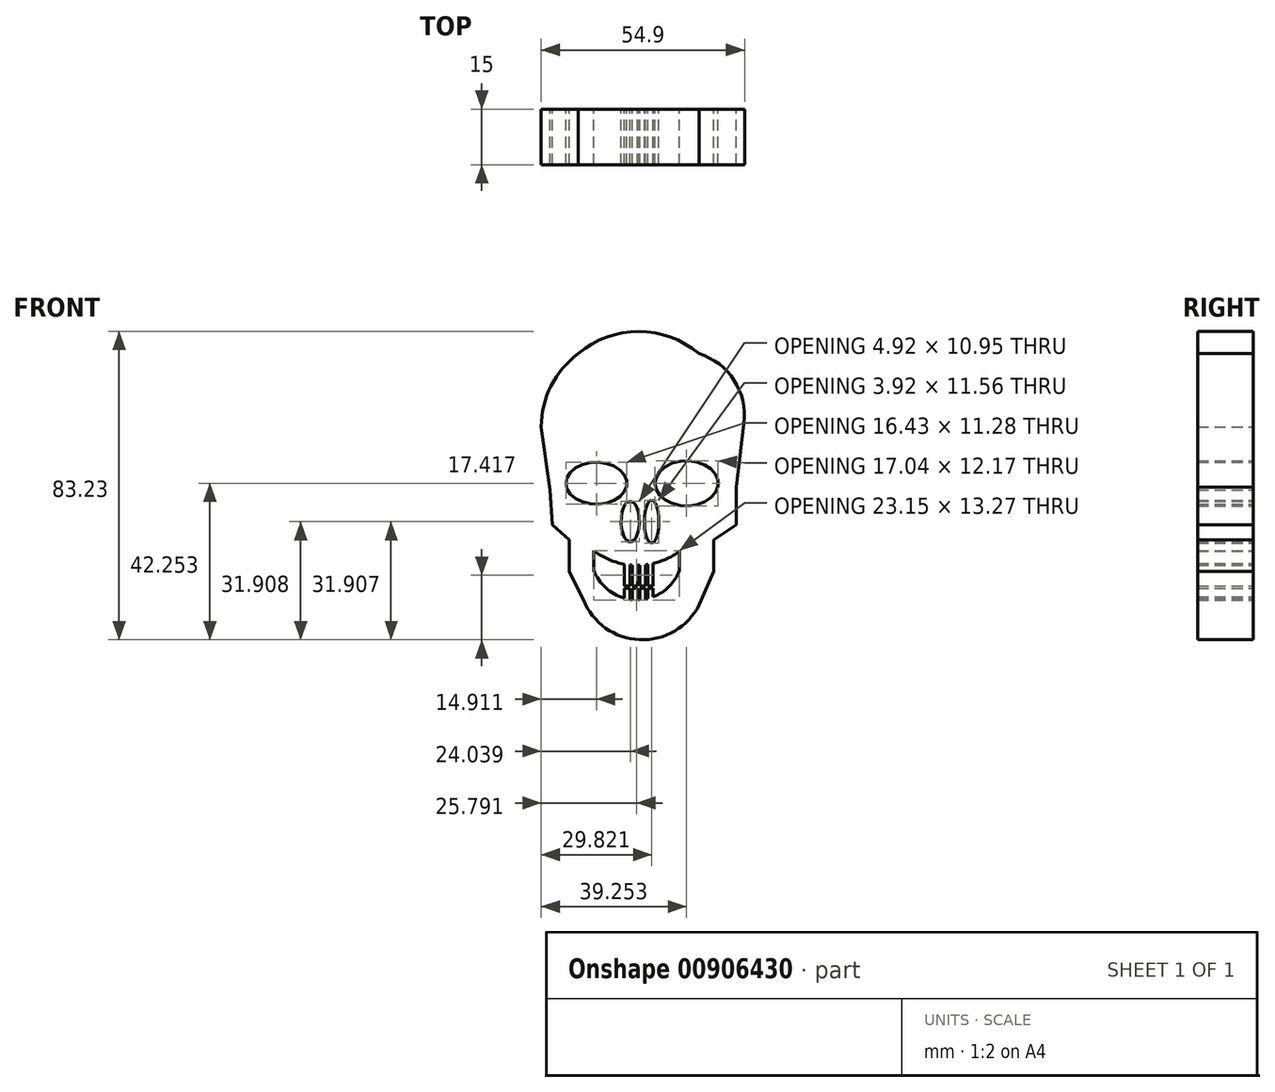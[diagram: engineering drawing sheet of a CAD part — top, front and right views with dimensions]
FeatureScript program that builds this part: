
annotation { "Feature Type Name" : "Feature", "Feature Type Description" : "" }
export const myFeature = defineFeature(function(context is Context, id is Id, definition is map)
    precondition{}
    {
        {
            var Q0;
            Q0=qCreatedBy(makeId("Front.planeOp"),FACE);
            var sketch = newSketch(context, id + "F0", { "sketchPlane" : qUnion([Q0])});
            skArc(sketch, "E0", {"start": v(-11.85, 27.42) * mm, "mid": v(-19.21, 18.72) * mm, "end": v(-21.89, 7.64) * mm});
            skArc(sketch, "E1", {"start": v(20.71, 27.42) * mm, "mid": v(4.43, 33.4) * mm, "end": v(-11.85, 27.42) * mm});
            skArc(sketch, "E2", {"start": v(32.88, 8.55) * mm, "mid": v(30.21, 20.19) * mm, "end": v(20.71, 27.42) * mm});
            skLineSegment(sketch, "E3", {"start": v(-21.89, 7.64) * mm, "end": v(-19.45, -9.4) * mm});
            skLineSegment(sketch, "E4", {"start": v(32.88, 8.55) * mm, "end": v(30.78, -8.64) * mm});
            skArc(sketch, "E5", {"start": v(-10.02, -40.13) * mm, "mid": v(5.94, -49.82) * mm, "end": v(21.32, -39.22) * mm});
            skLineSegment(sketch, "E6", {"start": v(-14.28, -22.8) * mm, "end": v(-14.28, -31.31) * mm});
            skLineSegment(sketch, "E7", {"start": v(-14.28, -31.31) * mm, "end": v(-10.02, -40.13) * mm});
            skLineSegment(sketch, "E8", {"start": v(24.67, -22.8) * mm, "end": v(24.67, -31.31) * mm});
            skLineSegment(sketch, "E9", {"start": v(24.67, -31.31) * mm, "end": v(21.32, -39.22) * mm});
            skLineSegment(sketch, "E10", {"start": v(-13.98, 3.99) * mm, "end": v(-16.72, 11.9) * mm});
            skLineSegment(sketch, "E11", {"start": v(-16.72, 11.9) * mm, "end": v(-13.98, 3.99) * mm});
            skLineSegment(sketch, "E12", {"start": v(-13.98, 3.99) * mm, "end": v(-19.45, -9.4) * mm});
            skLineSegment(sketch, "E13", {"start": v(25.27, 3.99) * mm, "end": v(27.4, 11.9) * mm});
            skLineSegment(sketch, "E14", {"start": v(27.4, 11.9) * mm, "end": v(25.27, 3.99) * mm});
            skLineSegment(sketch, "E15", {"start": v(25.27, 3.99) * mm, "end": v(30.78, -8.64) * mm});
            skLineSegment(sketch, "E16", {"start": v(-14.28, -22.8) * mm, "end": v(-18.85, -18.84) * mm});
            skLineSegment(sketch, "E17", {"start": v(-19.45, -9.4) * mm, "end": v(-18.85, -18.84) * mm});
            skLineSegment(sketch, "E18", {"start": v(24.67, -22.8) * mm, "end": v(30.78, -18.84) * mm});
            skLineSegment(sketch, "E19", {"start": v(30.78, -8.64) * mm, "end": v(30.78, -18.84) * mm});
            skEllipse(sketch, "E20", {"center": v(17.36, -7.58) * mm, "majorRadius": 8.52 * mm, "minorRadius": 6.09 * mm, "majorAxis": v(-1, 0)});
            skEllipse(sketch, "E21", {"center": v(-6.98, -7.58) * mm, "majorRadius": 8.22 * mm, "minorRadius": 5.64 * mm, "majorAxis": v(-1, 0)});
            skPoint(sketch, "E21.centerSnap0", {"position": v(8.84, -7.58) * mm});
            skEllipse(sketch, "E22", {"center": v(7.93, -17.92) * mm, "majorRadius": 5.78 * mm, "minorRadius": 1.96 * mm, "majorAxis": v(0, 1)});
            skEllipse(sketch, "E23", {"center": v(2.15, -17.92) * mm, "majorRadius": 5.48 * mm, "minorRadius": 2.46 * mm, "majorAxis": v(0, 1)});
            skArc(sketch, "E24", {"start": v(-7.67, -25.78) * mm, "mid": v(3.88, -29.71) * mm, "end": v(15.47, -25.93) * mm});
            skLineSegment(sketch, "E25", {"start": v(-7.67, -25.78) * mm, "end": v(-7.67, -31.11) * mm});
            skLineSegment(sketch, "E26", {"start": v(15.47, -31.11) * mm, "end": v(15.47, -25.93) * mm});
            skArc(sketch, "E27", {"start": v(-7.67, -31.11) * mm, "mid": v(3.9, -39.05) * mm, "end": v(15.47, -31.11) * mm});
            skLineSegment(sketch, "E28", {"start": v(4.17, -29.71) * mm, "end": v(4.17, -35.27) * mm});
            skLineSegment(sketch, "E29", {"start": v(2.67, -35.27) * mm, "end": v(4.17, -35.27) * mm});
            skLineSegment(sketch, "E30", {"start": v(2.67, -35.27) * mm, "end": v(2.67, -29.67) * mm});
            skLineSegment(sketch, "E31", {"start": v(4.77, -29.7) * mm, "end": v(4.77, -35.27) * mm});
            skLineSegment(sketch, "E32", {"start": v(4.77, -35.27) * mm, "end": v(6.27, -35.27) * mm});
            skLineSegment(sketch, "E33", {"start": v(6.27, -35.27) * mm, "end": v(6.27, -29.58) * mm});
            skLineSegment(sketch, "E34", {"start": v(2.07, -29.62) * mm, "end": v(2.07, -35.27) * mm});
            skLineSegment(sketch, "E35", {"start": v(2.07, -35.27) * mm, "end": v(0.57, -35.27) * mm});
            skLineSegment(sketch, "E36", {"start": v(0.57, -35.27) * mm, "end": v(0.57, -29.4) * mm});
            skLineSegment(sketch, "E37", {"start": v(6.87, -29.5) * mm, "end": v(6.87, -35.27) * mm});
            skLineSegment(sketch, "E38", {"start": v(8.37, -35.27) * mm, "end": v(6.87, -35.27) * mm});
            skLineSegment(sketch, "E39", {"start": v(8.37, -35.27) * mm, "end": v(8.37, -29.21) * mm});
            skLineSegment(sketch, "E40", {"start": v(0.57, -38.6) * mm, "end": v(0.57, -35.87) * mm});
            skLineSegment(sketch, "E41", {"start": v(0.57, -35.87) * mm, "end": v(2.07, -35.87) * mm});
            skLineSegment(sketch, "E42", {"start": v(2.07, -35.87) * mm, "end": v(2.07, -38.92) * mm});
            skLineSegment(sketch, "E43", {"start": v(2.67, -39) * mm, "end": v(2.67, -35.87) * mm});
            skLineSegment(sketch, "E44", {"start": v(2.67, -35.87) * mm, "end": v(4.17, -35.87) * mm});
            skLineSegment(sketch, "E45", {"start": v(4.17, -35.87) * mm, "end": v(4.17, -39.05) * mm});
            skLineSegment(sketch, "E46", {"start": v(4.77, -35.87) * mm, "end": v(4.77, -39.02) * mm});
            skLineSegment(sketch, "E47", {"start": v(4.77, -35.87) * mm, "end": v(6.27, -35.87) * mm});
            skLineSegment(sketch, "E48", {"start": v(6.27, -35.87) * mm, "end": v(6.27, -38.82) * mm});
            skLineSegment(sketch, "E49", {"start": v(6.87, -38.7) * mm, "end": v(6.87, -35.87) * mm});
            skLineSegment(sketch, "E50", {"start": v(6.87, -35.87) * mm, "end": v(8.37, -35.87) * mm});
            skLineSegment(sketch, "E51", {"start": v(8.37, -35.87) * mm, "end": v(8.37, -38.22) * mm});
            skSolve(sketch);
        }
        {
            var Q0;
            Q0 = qSketchRegion(id + "F0", true);
            var Q1;
            {var subQ0=sQuery(id+"F0.wireOp",EDGE,"E34");Q1=makeQuery(id+"F0.imprint","IMPRINT",FACE,{"disambiguationData":[TD([[makeQuery(id+"F0.imprint","IMPRINT",EDGE,{"derivedFrom":subQ0}),-1.0]])]});}
            var Q2;
            {var subQ0=sQuery(id+"F0.wireOp",EDGE,"E28");Q2=makeQuery(id+"F0.imprint","IMPRINT",FACE,{"disambiguationData":[TD([[makeQuery(id+"F0.imprint","IMPRINT",EDGE,{"derivedFrom":subQ0}),-1.0]])]});}
            var Q3;
            {var subQ0=sQuery(id+"F0.wireOp",EDGE,"E31");Q3=makeQuery(id+"F0.imprint","IMPRINT",FACE,{"disambiguationData":[TD([[makeQuery(id+"F0.imprint","IMPRINT",EDGE,{"derivedFrom":subQ0}),1.0]])]});}
            var Q4;
            {var subQ0=sQuery(id+"F0.wireOp",EDGE,"E37");Q4=makeQuery(id+"F0.imprint","IMPRINT",FACE,{"disambiguationData":[TD([[makeQuery(id+"F0.imprint","IMPRINT",EDGE,{"derivedFrom":subQ0}),1.0]])]});}
            var Q5;
            {var subQ0=sQuery(id+"F0.wireOp",EDGE,"E49");Q5=makeQuery(id+"F0.imprint","IMPRINT",FACE,{"disambiguationData":[TD([[makeQuery(id+"F0.imprint","IMPRINT",EDGE,{"derivedFrom":subQ0}),-1.0]])]});}
            var Q6;
            {var subQ0=sQuery(id+"F0.wireOp",EDGE,"E46");Q6=makeQuery(id+"F0.imprint","IMPRINT",FACE,{"disambiguationData":[TD([[makeQuery(id+"F0.imprint","IMPRINT",EDGE,{"derivedFrom":subQ0}),1.0]])]});}
            var Q7;
            {var subQ0=sQuery(id+"F0.wireOp",EDGE,"E43");Q7=makeQuery(id+"F0.imprint","IMPRINT",FACE,{"disambiguationData":[TD([[makeQuery(id+"F0.imprint","IMPRINT",EDGE,{"derivedFrom":subQ0}),-1.0]])]});}
            var Q8;
            {var subQ0=sQuery(id+"F0.wireOp",EDGE,"E40");Q8=makeQuery(id+"F0.imprint","IMPRINT",FACE,{"disambiguationData":[TD([[makeQuery(id+"F0.imprint","IMPRINT",EDGE,{"derivedFrom":subQ0}),-1.0]])]});}
            extrude(context, id + "F1", {"entities" : qUnion([Q0, Q1, Q2, Q3, Q4, Q5, Q6, Q7, Q8]), "depth" : 15 * mm, "offsetDistance" : 25 * mm});
        }
    });
